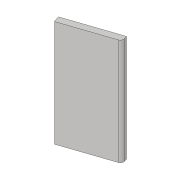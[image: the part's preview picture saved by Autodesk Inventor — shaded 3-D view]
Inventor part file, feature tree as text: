
AUTODESK INVENTOR PART (.ipt)
format: ipt  version: 2018.3 (Build 223284000, 284)  size: 77,824 bytes
history: native  units: in
note: dims shown in document units (in); Inventor stores cm internally (conversion verified against a paired STEP export)
features: extrude x1, fillet x1, sketch x1
ambient origin geometry x8: Origin, YZ Plane, XZ Plane, XY Plane, X Axis, Y Axis, Z Axis, Center Point
bodies: Solid1 (feature_tree)
feature tree (3):
  extrude  "Extrusion1"  Depth=1.925in TaperAngle=0.0deg
  fillet  "Fillet1"  Radius=0.116in
  sketch  "Sketch1"  dims[d0=0.975in d3=1.925in d4=0.0in d5=0.116in d6=0.0625in]
